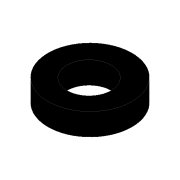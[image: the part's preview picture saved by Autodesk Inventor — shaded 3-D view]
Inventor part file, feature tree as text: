
AUTODESK INVENTOR PART (.ipt)
format: ipt  version: 2018 (Build 220112000, 112)  size: 83,968 bytes
history: native  units: mm
features: extrude x1, sketch x1
ambient origin geometry x8: Origin, YZ Plane, XZ Plane, XY Plane, X Axis, Y Axis, Z Axis, Center Point
bodies: Solid1 (feature_tree)
feature tree (2):
  extrude  "Extrusion1"  Depth=10.0mm
  sketch  "Sketch1"  dims[d0=19.0mm d1=10.0mm d2=5.0mm d3=0.0mm]
